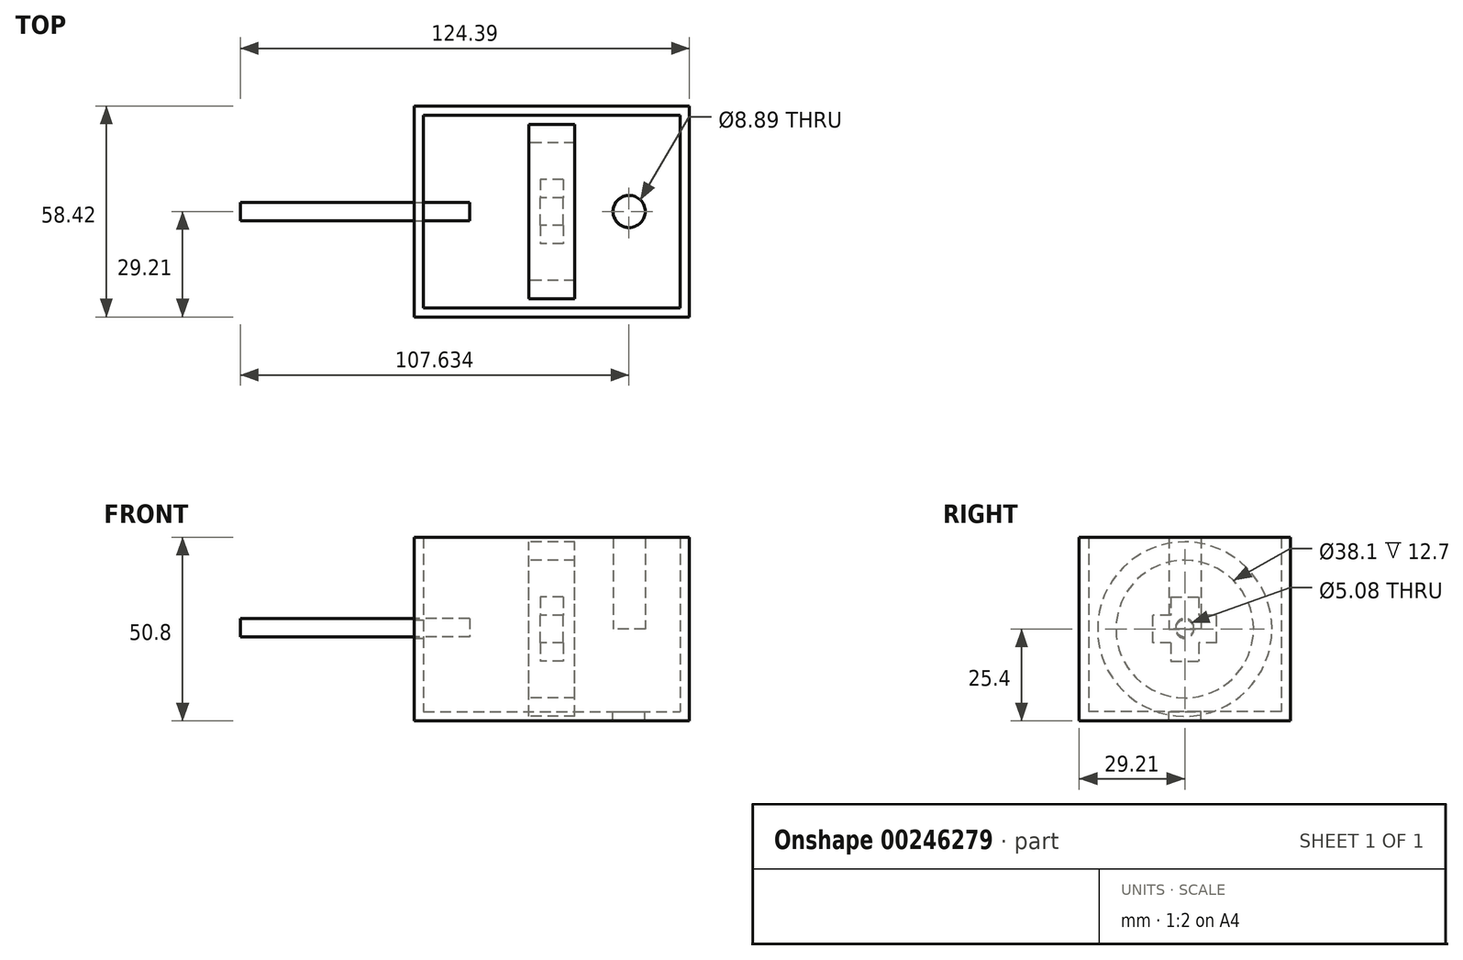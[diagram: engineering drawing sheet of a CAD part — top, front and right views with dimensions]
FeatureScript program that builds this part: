
annotation { "Feature Type Name" : "Feature", "Feature Type Description" : "" }
export const myFeature = defineFeature(function(context is Context, id is Id, definition is map)
    precondition{}
    {
        {
            var Q0;
            Q0=qCreatedBy(makeId("Front.planeOp"),FACE);
            var sketch = newSketch(context, id + "F0", { "sketchPlane" : qUnion([Q0])});
            skLineSegment(sketch, "E0.bottom", {"start": v(-38.1, 25.4) * mm, "end": v(38.1, 25.4) * mm});
            skLineSegment(sketch, "E0.top", {"start": v(-38.1, -25.4) * mm, "end": v(38.1, -25.4) * mm});
            skLineSegment(sketch, "E0.left", {"start": v(-38.1, 25.4) * mm, "end": v(-38.1, -25.4) * mm});
            skLineSegment(sketch, "E0.right", {"start": v(38.1, 25.4) * mm, "end": v(38.1, -25.4) * mm});
            skPoint(sketch, "E0.middle", {"position": v(0, 0) * mm});
            skSolve(sketch);
        }
        {
            var Q0;
            Q0 = qSketchRegion(id + "F0", true);
            extrude(context, id + "F1", {"entities" : qUnion([Q0]), "endBound" : BoundingType.SYMMETRIC, "oppositeDirection" : true, "depth" : 58.42 * mm});
        }
        {
            var Q0;
            Q0=makeQuery(id+"F1.opExtrude","SWEPT_FACE",FACE,{"disambiguationData":[OSD([sQuery(id+"F0.wireOp",EDGE,"E0.bottom")])]});
            var Q1;
            Q1=makeQuery(id+"F1.opExtrude","SWEPT_BODY",BODY,{"disambiguationData":[OSD([sQuery(id+"F0.wireOp",EDGE,"E0.bottom"),sQuery(id+"F0.wireOp",EDGE,"E0.top"),sQuery(id+"F0.wireOp",EDGE,"E0.left"),sQuery(id+"F0.wireOp",EDGE,"E0.right")])]});
            shell(context, id + "F2", {"entities" : qUnion([Q0]), "parts" : qUnion([Q1]), "thickness" : 2.54 * mm});
        }
        {
            var Q0;
            Q0=qCreatedBy(makeId("Right.planeOp"),FACE);
            var sketch = newSketch(context, id + "F3", { "sketchPlane" : qUnion([Q0])});
            skCircle(sketch, "E1", {"center": v(0, 0) * mm, "radius": 2.54 * mm});
            skSolve(sketch);
        }
        {
            var Q0;
            Q0 = qSketchRegion(id + "F3", true);
            extrude(context, id + "F4", {"entities" : qUnion([Q0]), "operationType" : NewBodyOperationType.REMOVE, "endBound" : BoundingType.THROUGH_ALL, "oppositeDirection" : true, "depth" : 25.4 * mm});
        }
        {
            var Q0;
            Q0=qCreatedBy(makeId("Front.planeOp"),FACE);
            var sketch = newSketch(context, id + "F5", { "sketchPlane" : qUnion([Q0])});
            skLineSegment(sketch, "E2.bottom", {"start": v(-22.79, 0.42) * mm, "end": v(-86.29, 0.42) * mm});
            skLineSegment(sketch, "E2.top", {"start": v(-22.79, 2.96) * mm, "end": v(-86.29, 2.96) * mm});
            skLineSegment(sketch, "E2.left", {"start": v(-22.79, 0.42) * mm, "end": v(-22.79, 2.96) * mm});
            skLineSegment(sketch, "E2.right", {"start": v(-86.29, 0.42) * mm, "end": v(-86.29, 2.96) * mm});
            skPoint(sketch, "E2.middle", {"position": v(-54.54, 1.7) * mm});
            skLineSegment(sketch, "E3", {"start": v(-92, 0.42) * mm, "end": v(-30.07, 0.42) * mm, "construction": true});
            skSolve(sketch);
        }
        {
            var Q0;
            Q0 = qSketchRegion(id + "F5", true);
            var Q1;
            Q1=sQuery(id+"F5.wireOp",EDGE,"E3");
            revolve(context, id + "F6", {"entities" : qUnion([Q0]), "axis" : qUnion([Q1]), "revolveType" : RevolveType.FULL});
        }
        {
            var Q0;
            Q0=qCreatedBy(makeId("Right.planeOp"),FACE);
            var sketch = newSketch(context, id + "F7", { "sketchPlane" : qUnion([Q0])});
            skLineSegment(sketch, "E4.bottom", {"start": v(-3.81, 8.9) * mm, "end": v(3.81, 8.9) * mm});
            skLineSegment(sketch, "E4.top", {"start": v(-3.81, -8.89) * mm, "end": v(3.8, -8.89) * mm});
            skLineSegment(sketch, "E4.left", {"start": v(-3.81, 8.9) * mm, "end": v(-3.81, -8.89) * mm});
            skLineSegment(sketch, "E4.right", {"start": v(3.81, 8.9) * mm, "end": v(3.8, -8.9) * mm});
            skPoint(sketch, "E4.middle", {"position": v(0, 0) * mm});
            skLineSegment(sketch, "E5.bottom", {"start": v(8.9, -3.81) * mm, "end": v(-8.9, -3.81) * mm});
            skLineSegment(sketch, "E5.top", {"start": v(8.9, 3.81) * mm, "end": v(-8.9, 3.8) * mm});
            skLineSegment(sketch, "E5.left", {"start": v(8.9, -3.81) * mm, "end": v(8.9, 3.8) * mm});
            skLineSegment(sketch, "E5.right", {"start": v(-8.9, -3.81) * mm, "end": v(-8.9, 3.8) * mm});
            skSolve(sketch);
        }
        {
            var Q0;
            Q0 = qSketchRegion(id + "F7", true);
            extrude(context, id + "F8", {"entities" : qUnion([Q0]), "endBound" : BoundingType.SYMMETRIC, "depth" : 6.35 * mm});
        }
        {
            var Q0;
            Q0=qCreatedBy(makeId("Right.planeOp"),FACE);
            var sketch = newSketch(context, id + "F9", { "sketchPlane" : qUnion([Q0])});
            skCircle(sketch, "E6", {"center": v(0, 0) * mm, "radius": 24.13 * mm});
            skCircle(sketch, "E7", {"center": v(0, 0) * mm, "radius": 19.05 * mm});
            skSolve(sketch);
        }
        {
            var Q0;
            Q0 = qSketchRegion(id + "F9", true);
            extrude(context, id + "F10", {"entities" : qUnion([Q0]), "endBound" : BoundingType.SYMMETRIC, "depth" : 12.7 * mm});
        }
        {
            var Q0;
            Q0=qCreatedBy(makeId("Top.planeOp"),FACE);
            var sketch = newSketch(context, id + "F11", { "sketchPlane" : qUnion([Q0])});
            skCircle(sketch, "E8", {"center": v(21.34, 0) * mm, "radius": 4.45 * mm});
            skSolve(sketch);
        }
        {
            var Q0;
            Q0 = qSketchRegion(id + "F11", true);
            extrude(context, id + "F12", {"entities" : qUnion([Q0]), "operationType" : NewBodyOperationType.REMOVE, "oppositeDirection" : true, "depth" : 41.66 * mm});
        }
        {
            var Q0;
            Q0=qCreatedBy(makeId("Top.planeOp"),FACE);
            var sketch = newSketch(context, id + "F13", { "sketchPlane" : qUnion([Q0])});
            skCircle(sketch, "E9", {"center": v(21.38, 0) * mm, "radius": 4.45 * mm});
            skSolve(sketch);
        }
        {
            var Q0;
            Q0 = qSketchRegion(id + "F13", true);
            extrude(context, id + "F14", {"entities" : qUnion([Q0]), "depth" : 25.4 * mm});
        }
    });
